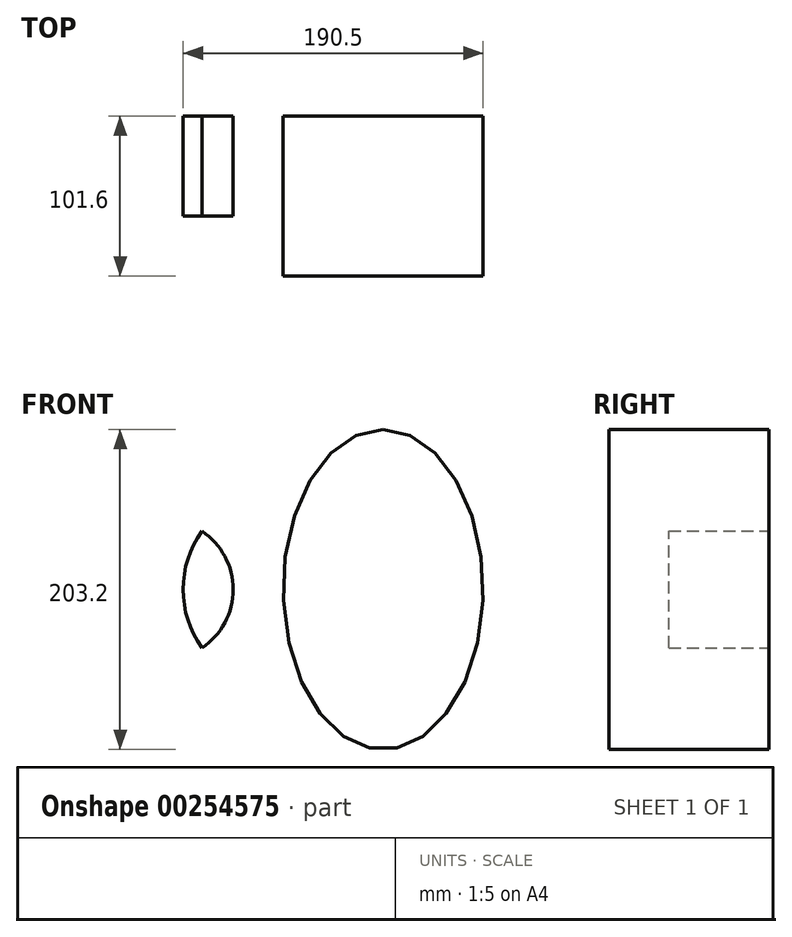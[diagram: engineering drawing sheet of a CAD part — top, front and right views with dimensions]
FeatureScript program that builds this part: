
annotation { "Feature Type Name" : "Feature", "Feature Type Description" : "" }
export const myFeature = defineFeature(function(context is Context, id is Id, definition is map)
    precondition{}
    {
        {
            var Q0;
            Q0=qCreatedBy(makeId("Front.planeOp"),FACE);
            var sketch = newSketch(context, id + "F0", { "sketchPlane" : qUnion([Q0])});
            skLineSegment(sketch, "E0", {"start": v(0, 0) * mm, "end": v(-76.2, 0) * mm});
            skCircle(sketch, "E1", {"center": v(-76.2, 0) * mm, "radius": 44.45 * mm});
            skLineSegment(sketch, "E2", {"start": v(-31.75, 0) * mm, "end": v(-63.5, 0) * mm});
            skCircle(sketch, "E3", {"center": v(0, 0) * mm, "radius": 63.5 * mm});
            skLineSegment(sketch, "E4", {"start": v(63.5, 0) * mm, "end": v(63.5, 101.6) * mm});
            skEllipse(sketch, "E5", {"center": v(63.5, 0) * mm, "majorRadius": 101.6 * mm, "minorRadius": 63.5 * mm, "majorAxis": v(0, 1)});
            skSolve(sketch);
        }
        {
            var Q0;
            {var subQ0=sQuery(id+"F0.wireOp",EDGE,"E3");var subQ1=sQuery(id+"F0.wireOp",EDGE,"E1");var subQ2=makeQuery(id+"F0.imprint","INTERSECT",VERTEX,{"disambiguationData":[OD(0.0)],"derivedFrom":[subQ1,subQ0]});Q0=makeQuery(id+"F0.imprint","IMPRINT",FACE,{"disambiguationData":[TD([[makeQuery(id+"F0.imprint","IMPRINT",EDGE,{"disambiguationData":[TD([[subQ2,-1.0]])],"derivedFrom":subQ1}),1.0]])]});}
            extrude(context, id + "F1", {"entities" : qUnion([Q0]), "depth" : 25.4 * mm});
        }
        {
            var Q0;
            {var subQ3=sQuery(id+"F0.wireOp",EDGE,"E1");var subQ5=sQuery(id+"F0.wireOp",EDGE,"E3");var subQ6=makeQuery(id+"F0.imprint","INTERSECT",VERTEX,{"disambiguationData":[OD(0.0)],"derivedFrom":[subQ3,subQ5]});Q0=makeQuery(id+"F0.imprint","IMPRINT",FACE,{"disambiguationData":[TD([[makeQuery(id+"F0.imprint","IMPRINT",EDGE,{"disambiguationData":[TD([[subQ6,1.0]])],"derivedFrom":subQ5}),1.0]])]});}
            var Q1;
            {var subQ0=sQuery(id+"F0.wireOp",EDGE,"E2");Q1=makeQuery(id+"F0.imprint","IMPRINT",FACE,{"disambiguationData":[TD([[makeQuery(id+"F0.imprint","IMPRINT",EDGE,{"derivedFrom":subQ0}),-1.0]])]});}
            var Q2;
            {var subQ0=sQuery(id+"F0.wireOp",EDGE,"E2");Q2=makeQuery(id+"F0.imprint","IMPRINT",FACE,{"disambiguationData":[TD([[makeQuery(id+"F0.imprint","IMPRINT",EDGE,{"derivedFrom":subQ0}),1.0]])]});}
            var Q3;
            {var subQ3=sQuery(id+"F0.wireOp",EDGE,"E1");var subQ5=sQuery(id+"F0.wireOp",EDGE,"E3");var subQ6=makeQuery(id+"F0.imprint","INTERSECT",VERTEX,{"disambiguationData":[OD(1.0)],"derivedFrom":[subQ3,subQ5]});Q3=makeQuery(id+"F0.imprint","IMPRINT",FACE,{"disambiguationData":[TD([[makeQuery(id+"F0.imprint","IMPRINT",EDGE,{"disambiguationData":[TD([[subQ6,-1.0]])],"derivedFrom":subQ5}),1.0]])]});}
            extrude(context, id + "F2", {"entities" : qUnion([Q0, Q1, Q2, Q3]), "operationType" : NewBodyOperationType.ADD, "depth" : 63.5 * mm});
        }
        {
            var Q0;
            {var subQ0=sQuery(id+"F0.wireOp",EDGE,"E3");var subQ1=makeQuery(id+"F0.imprint","INTERSECT",VERTEX,{"derivedFrom":[subQ0,sQuery(id+"F0.wireOp",EDGE,"E4")]});Q0=makeQuery(id+"F0.imprint","IMPRINT",FACE,{"disambiguationData":[TD([[makeQuery(id+"F0.imprint","IMPRINT",EDGE,{"disambiguationData":[TD([[subQ1,-1.0]])],"derivedFrom":subQ0}),1.0]])]});}
            var Q1;
            {var subQ0=sQuery(id+"F0.wireOp",EDGE,"E4");Q1=makeQuery(id+"F0.imprint","IMPRINT",FACE,{"disambiguationData":[TD([[makeQuery(id+"F0.imprint","IMPRINT",EDGE,{"derivedFrom":subQ0}),1.0]])]});}
            var Q2;
            {var subQ0=sQuery(id+"F0.wireOp",EDGE,"E4");Q2=makeQuery(id+"F0.imprint","IMPRINT",FACE,{"disambiguationData":[TD([[makeQuery(id+"F0.imprint","IMPRINT",EDGE,{"derivedFrom":subQ0}),-1.0]])]});}
            extrude(context, id + "F3", {"entities" : qUnion([Q0, Q1, Q2]), "operationType" : NewBodyOperationType.ADD, "depth" : 101.6 * mm});
        }
    });
